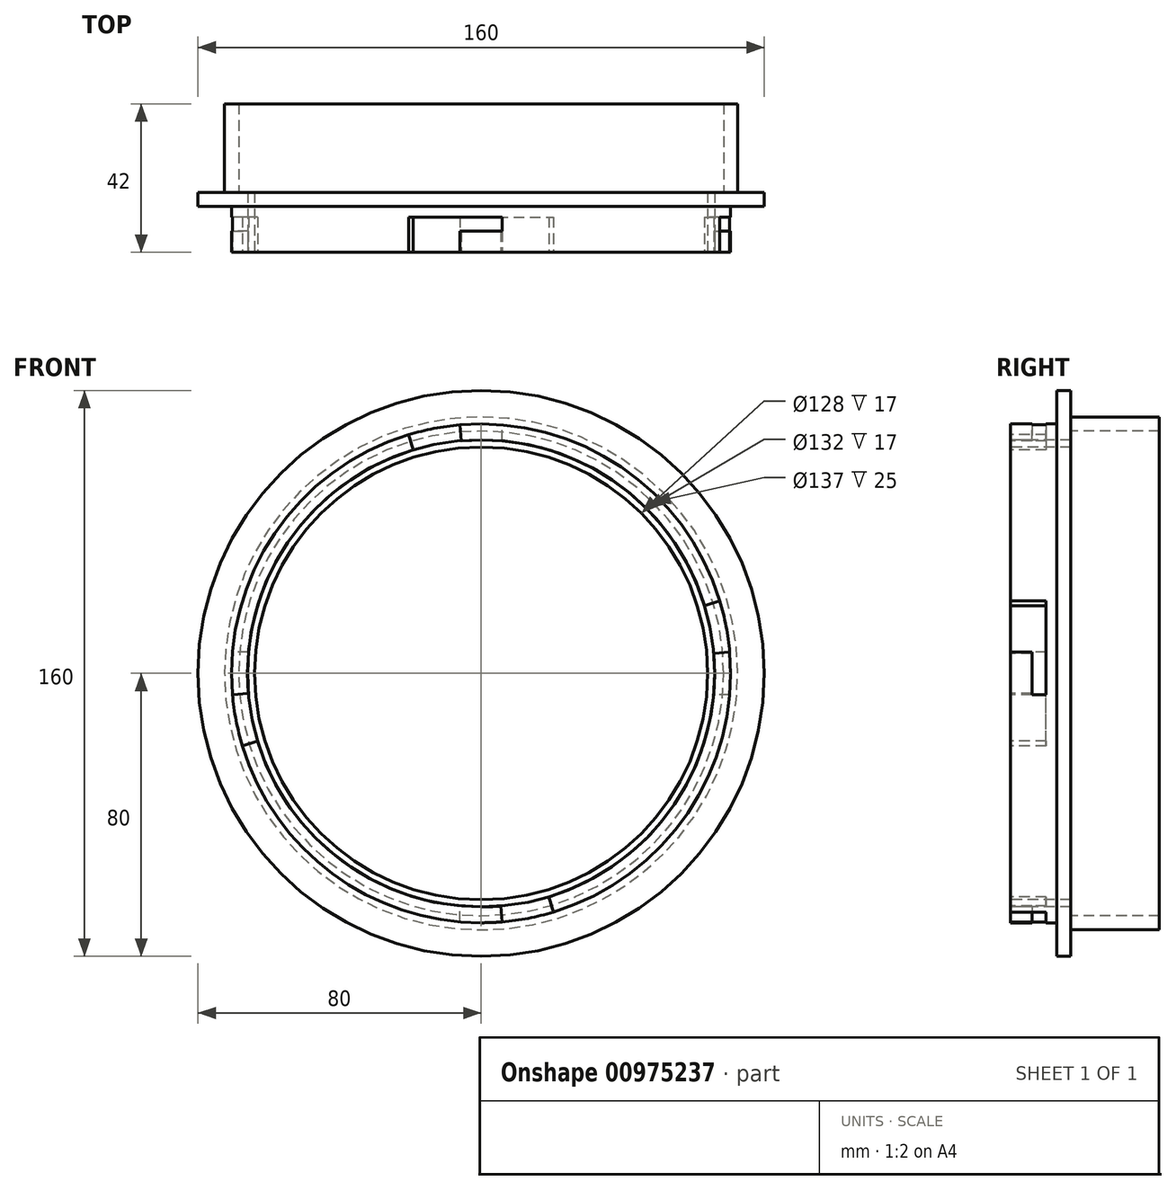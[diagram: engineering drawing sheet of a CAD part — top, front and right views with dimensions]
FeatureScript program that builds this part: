
annotation { "Feature Type Name" : "Feature", "Feature Type Description" : "" }
export const myFeature = defineFeature(function(context is Context, id is Id, definition is map)
    precondition{}
    {
        {
            var Q0;
            Q0=qCreatedBy(makeId("Front.planeOp"),FACE);
            var sketch = newSketch(context, id + "F0", { "sketchPlane" : qUnion([Q0])});
            skCircle(sketch, "E0", {"center": v(0, 0) * mm, "radius": 70.5 * mm});
            skCircle(sketch, "E1", {"center": v(0, 0) * mm, "radius": 66 * mm});
            skSolve(sketch);
        }
        {
            var Q0;
            Q0=makeQuery(id+"F0.imprint","IMPRINT",FACE,{"disambiguationData":[TD([[makeQuery(id+"F0.imprint","IMPRINT",EDGE,{"derivedFrom":sQuery(id+"F0.wireOp",EDGE,"E0")}),1.0]])]});
            extrude(context, id + "F1", {"entities" : qUnion([Q0]), "oppositeDirection" : true, "depth" : 13 * mm, "offsetDistance" : 25 * mm});
        }
        {
            var Q0;
            Q0=makeQuery(id+"F1.opExtrude","CAP_FACE",FACE,{"disambiguationData":[OSD([sQuery(id+"F0.wireOp",EDGE,"E0"),sQuery(id+"F0.wireOp",EDGE,"E1")])],"isStart":false});
            var sketch = newSketch(context, id + "F2", { "sketchPlane" : qUnion([Q0])});
            skCircle(sketch, "E2", {"center": v(0, 0) * mm, "radius": 80 * mm});
            skSolve(sketch);
        }
        {
            var Q0;
            Q0=makeQuery(id+"F2.imprint","IMPRINT",FACE,{"disambiguationData":[TD([[makeQuery(id+"F2.imprint","IMPRINT",EDGE,{"derivedFrom":sQuery(id+"F2.wireOp",EDGE,"E2")}),1.0]])]});
            var Q1;
            Q1=makeQuery(id+"F2.imprint","IMPRINT",FACE,{"disambiguationData":[TD([[makeQuery(id+"F2.imprint","IMPRINT",EDGE,{"derivedFrom":makeQuery(id+"F1.opExtrude","CAP_EDGE",EDGE,{"disambiguationData":[OSD([sQuery(id+"F0.wireOp",EDGE,"E0")])],"isStart":false})}),-1.0]])]});
            extrude(context, id + "F3", {"entities" : qUnion([Q0, Q1]), "operationType" : NewBodyOperationType.ADD, "depth" : 4 * mm, "offsetDistance" : 25 * mm});
        }
        {
            var Q0;
            Q0=qCreatedBy(makeId("Top.planeOp"),FACE);
            var sketch = newSketch(context, id + "F4", { "sketchPlane" : qUnion([Q0])});
            skLineSegment(sketch, "E3", {"start": v(0, 10) * mm, "end": v(6, 10) * mm});
            skLineSegment(sketch, "E4.MirrorCS", {"start": v(0, 10) * mm, "end": v(-6, 10) * mm});
            skLineSegment(sketch, "E5", {"start": v(-6, 10) * mm, "end": v(-6, 6) * mm});
            skLineSegment(sketch, "E6", {"start": v(-6, 6) * mm, "end": v(6, 6) * mm});
            skLineSegment(sketch, "E7", {"start": v(6, 6) * mm, "end": v(6, 10) * mm});
            skSolve(sketch);
        }
        {
            var Q0;
            Q0=makeQuery(id+"F4.imprint","IMPRINT",FACE,{"disambiguationData":[TD([[makeQuery(id+"F4.imprint","IMPRINT",EDGE,{"derivedFrom":sQuery(id+"F4.wireOp",EDGE,"E3")}),-1.0]])]});
            extrude(context, id + "F5", {"entities" : qUnion([Q0]), "operationType" : NewBodyOperationType.REMOVE, "endBound" : BoundingType.SYMMETRIC, "oppositeDirection" : true, "depth" : 160 * mm, "offsetDistance" : 25 * mm});
        }
        {
            var Q0;
            Q0=qCreatedBy(makeId("Right.planeOp"),FACE);
            var sketch = newSketch(context, id + "F6", { "sketchPlane" : qUnion([Q0])});
            skLineSegment(sketch, "E8", {"start": v(10, 0) * mm, "end": v(10, 6) * mm});
            skLineSegment(sketch, "E9", {"start": v(10, 6) * mm, "end": v(6, 6) * mm});
            skLineSegment(sketch, "E10", {"start": v(6, 6) * mm, "end": v(6, 0) * mm});
            skLineSegment(sketch, "E11.MirrorCS", {"start": v(6, -6) * mm, "end": v(6, 0) * mm});
            skLineSegment(sketch, "E12.MirrorCS", {"start": v(10, -6) * mm, "end": v(6, -6) * mm});
            skLineSegment(sketch, "E13.MirrorCS", {"start": v(10, 0) * mm, "end": v(10, -6) * mm});
            skSolve(sketch);
        }
        {
            var Q0;
            Q0=makeQuery(id+"F6.imprint","IMPRINT",FACE,{"disambiguationData":[TD([[makeQuery(id+"F6.imprint","IMPRINT",EDGE,{"derivedFrom":sQuery(id+"F6.wireOp",EDGE,"E8")}),1.0]])]});
            extrude(context, id + "F7", {"entities" : qUnion([Q0]), "operationType" : NewBodyOperationType.REMOVE, "endBound" : BoundingType.SYMMETRIC, "depth" : 160 * mm, "offsetDistance" : 25 * mm});
        }
        {
            var Q0;
            Q0=qCreatedBy(makeId("Front.planeOp"),FACE);
            var sketch = newSketch(context, id + "F8", { "sketchPlane" : qUnion([Q0])});
            skLineSegment(sketch, "E14", {"start": v(-6.4, 75.15) * mm, "end": v(0, 0) * mm});
            skLineSegment(sketch, "E15", {"start": v(0, 0) * mm, "end": v(6.4, -75.09) * mm});
            skLineSegment(sketch, "E16", {"start": v(-21.63, 71.3) * mm, "end": v(0, 0) * mm});
            skLineSegment(sketch, "E17", {"start": v(0, 0) * mm, "end": v(21.76, -71.72) * mm});
            skLineSegment(sketch, "E18", {"start": v(-6.4, 75.15) * mm, "end": v(-21.63, 71.3) * mm});
            skLineSegment(sketch, "E19", {"start": v(6.4, -75.09) * mm, "end": v(21.76, -71.72) * mm});
            skLineSegment(sketch, "E20", {"start": v(75.79, 6.45) * mm, "end": v(0, 0) * mm});
            skLineSegment(sketch, "E21", {"start": v(0, 0) * mm, "end": v(-74.84, -6.37) * mm});
            skLineSegment(sketch, "E22", {"start": v(71.43, 21.67) * mm, "end": v(-80.51, -24.42) * mm});
            skLineSegment(sketch, "E23", {"start": v(-74.84, -6.37) * mm, "end": v(-80.51, -24.42) * mm});
            skLineSegment(sketch, "E24", {"start": v(71.43, 21.67) * mm, "end": v(75.79, 6.45) * mm});
            skSolve(sketch);
        }
        {
            var Q0;
            Q0 = qSketchRegion(id + "F8", true);
            extrude(context, id + "F9", {"entities" : qUnion([Q0]), "operationType" : NewBodyOperationType.REMOVE, "oppositeDirection" : true, "depth" : 10 * mm, "offsetDistance" : 25 * mm});
        }
        {
            var Q0;
            Q0=makeQuery(id+"F3.opExtrude","CAP_FACE",FACE,{"disambiguationData":[OSD([sQuery(id+"F0.wireOp",EDGE,"E1"),sQuery(id+"F2.wireOp",EDGE,"E2")])],"isStart":false});
            var sketch = newSketch(context, id + "F10", { "sketchPlane" : qUnion([Q0])});
            skCircle(sketch, "E25", {"center": v(0, 0) * mm, "radius": 72.5 * mm});
            skCircle(sketch, "E26", {"center": v(0, 0) * mm, "radius": 68.5 * mm});
            skSolve(sketch);
        }
        {
            var Q0;
            Q0 = qSketchRegion(id + "F10", true);
            extrude(context, id + "F11", {"entities" : qUnion([Q0]), "operationType" : NewBodyOperationType.ADD, "depth" : 25 * mm, "offsetDistance" : 25 * mm});
        }
        {
            var Q0;
            {var subQ0=sQuery(id+"F0.wireOp",EDGE,"E1");var subQ1=sQuery(id+"F8.wireOp",EDGE,"E15");var subQ2=sQuery(id+"F0.wireOp",EDGE,"E0");Q0=makeQuery(id+"F9.boolean.opBoolean","SPLIT",FACE,{"disambiguationData":[TD([makeQuery(id+"F9.opExtrude","SWEPT_FACE",FACE,{"disambiguationData":[OSD([subQ1])]})])],"derivedFrom":makeQuery(id+"F1.opExtrude","CAP_FACE",FACE,{"disambiguationData":[OSD([subQ2,subQ0])],"isStart":true})});}
            var sketch = newSketch(context, id + "F12", { "sketchPlane" : qUnion([Q0])});
            skCircle(sketch, "E27", {"center": v(0, 0) * mm, "radius": 66 * mm});
            skCircle(sketch, "E28", {"center": v(0, 0) * mm, "radius": 64 * mm});
            skSolve(sketch);
        }
        {
            var Q0;
            Q0=makeQuery(id+"F12.imprint","IMPRINT",FACE,{"disambiguationData":[TD([[makeQuery(id+"F12.imprint","IMPRINT",EDGE,{"derivedFrom":sQuery(id+"F12.wireOp",EDGE,"E27")}),1.0]])]});
            extrude(context, id + "F13", {"entities" : qUnion([Q0]), "oppositeDirection" : true, "depth" : 17 * mm, "offsetDistance" : 25 * mm});
        }
    });
